# Revit family: NoiseBREAK (R2.7)
name_source: partatom
category: Structural Stiffeners
units: mm (PartAtom-declared; Revit-internal decimal feet)

## family parameters
Cut with Voids When Loaded = No
OmniClass Number = 23.25.30.11.27
OmniClass Title = Vibration and Earthquake Controls
Shared = No

## types (1)
- R2.7 - NoiseBREAK
    Density = 32.00 kg/m³
    Description = Ecowool NoiseBREAK is semi-rigid or rigid slabs of non-combustible, water repellent, glass mineral wool. They are designed to suit internal walls and ceiling of residential, commercial and industrial buildings. Excellent thermal, acoustic and fire safety performance.
    ECOWOOL Product thickness in mm = 90mm x 32kg/m3
    Finish = NoiseBREAK
    Gypsum Thickness (mm) = 13 mm
    Height Wall (mm) = 2500 mm  [stored 8.2021 ft]
    Insulation Length (mm) = 609 mm  [stored 1.99803 ft]
    Insulation Thickness (mm) = 90 mm  [stored 0.295276 ft]
    Manufacturer = PGF Insulation Sdn. Bhd.
    Metal Stud Spacer (mm) = 609 mm  [stored 1.99803 ft]
    Metal Stud Width = 90 mm  [stored 0.295276 ft]
    Model = NoiseBREAK
    Thermal K Value = 0.0327
    Thermal R Value = 2.7
    Total System Thickness-mm = 90 mm  [stored 0.295276 ft]
    Type of Insulation = Glass Mineral Wool Blanket with vapour barrier
    Typical weight of ECOWOOL-Kg/M2 = 0 mm  [stored 0 ft]
    U-Value W/m2k = 0 mm  [stored 0 ft]
    URL = www.ecowool.com.my

note: [stored X ft] marks values corroborated as IEEE doubles in the binary element streams (Revit-internal decimal feet)

## geometry (parser evidence)
native form markers: Sweep x15
no freeform markers — native parametric forms only
